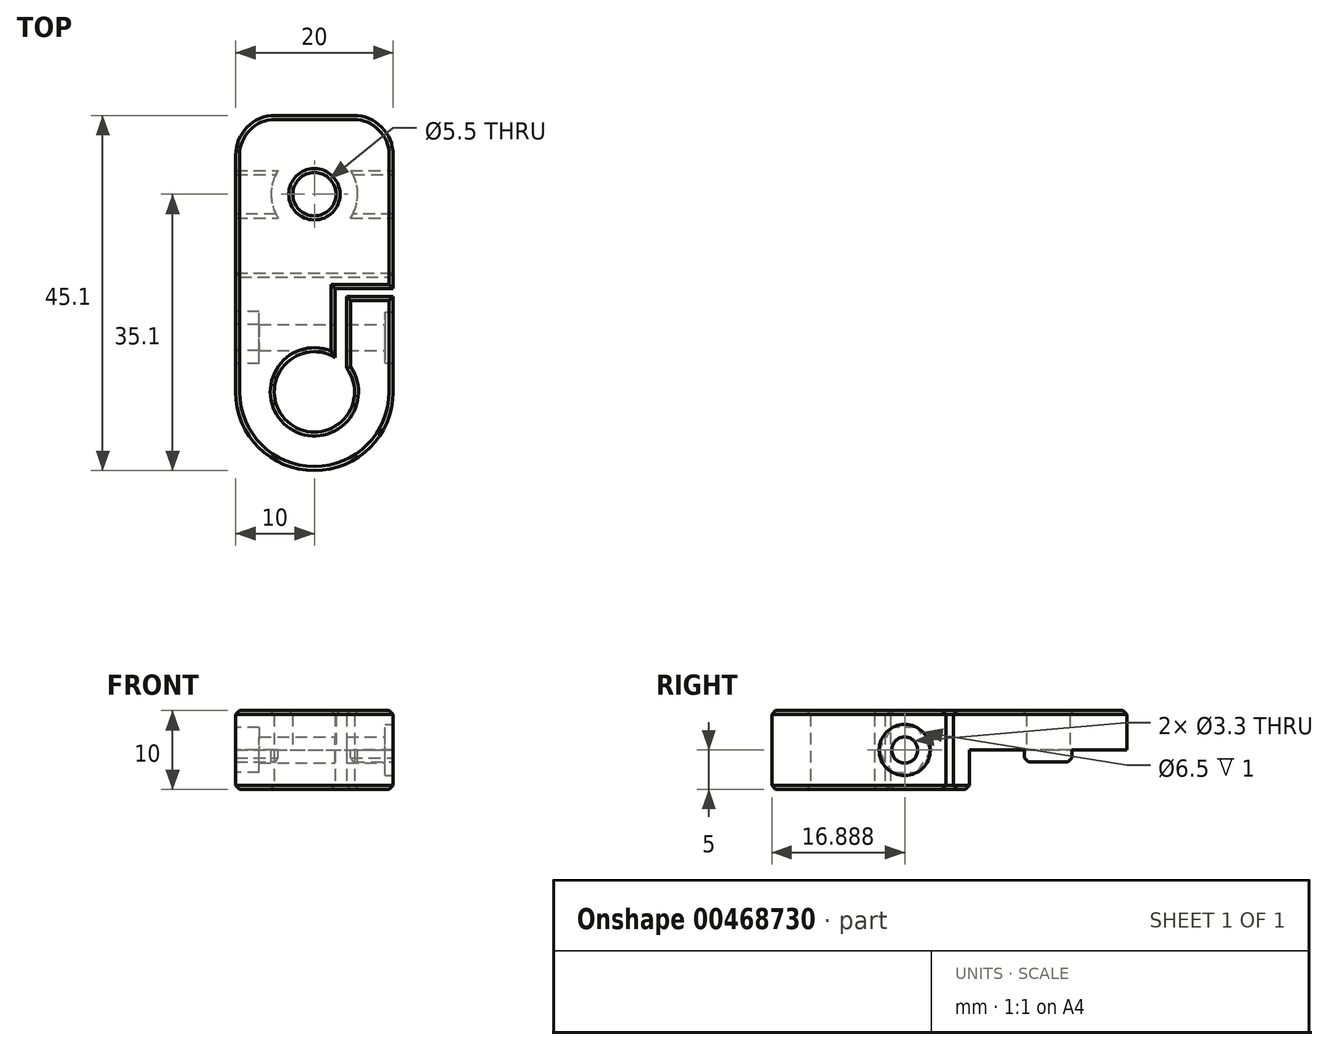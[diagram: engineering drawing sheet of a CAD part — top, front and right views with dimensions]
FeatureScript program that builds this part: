
annotation { "Feature Type Name" : "Feature", "Feature Type Description" : "" }
export const myFeature = defineFeature(function(context is Context, id is Id, definition is map)
    precondition{}
    {
        {
            var Q0;
            Q0=qCreatedBy(makeId("Top.planeOp"),FACE);
            var sketch = newSketch(context, id + "F0", { "sketchPlane" : qUnion([Q0])});
            skLineSegment(sketch, "E0.bottom", {"start": v(-50, 0) * mm, "end": v(50, 0) * mm, "construction": true});
            skLineSegment(sketch, "E0.top", {"start": v(-50, -20) * mm, "end": v(50, -20) * mm, "construction": true});
            skLineSegment(sketch, "E0.left", {"start": v(-50, 0) * mm, "end": v(-50, -20) * mm, "construction": true});
            skLineSegment(sketch, "E0.right", {"start": v(50, 0) * mm, "end": v(50, -20) * mm, "construction": true});
            skLineSegment(sketch, "E1.bottom", {"start": v(-10, 0) * mm, "end": v(10, 0) * mm});
            skLineSegment(sketch, "E1.top", {"start": v(0, -45.1) * mm, "end": v(0, -45.1) * mm});
            skLineSegment(sketch, "E1.left", {"start": v(-10, 0) * mm, "end": v(-10, -35.1) * mm});
            skLineSegment(sketch, "E1.right", {"start": v(10, 0) * mm, "end": v(10, -22) * mm});
            skArc(sketch, "E2", {"start": v(2.6, -30.71) * mm, "mid": v(-3.42, -38.89) * mm, "end": v(4.1, -32.07) * mm});
            skLineSegment(sketch, "E3", {"start": v(-10, -45.1) * mm, "end": v(10, -25.1) * mm, "construction": true});
            skPoint(sketch, "E4.visualSharp", {"position": v(-10, -45.1) * mm});
            skArc(sketch, "E4.filletArc", {"start": v(-10, -35.1) * mm, "mid": v(-7.07, -42.17) * mm, "end": v(0, -45.1) * mm});
            skPoint(sketch, "E5.visualSharp", {"position": v(10, -45.1) * mm});
            skArc(sketch, "E5.filletArc", {"start": v(0, -45.1) * mm, "mid": v(7.07, -42.17) * mm, "end": v(10, -35.1) * mm});
            skLineSegment(sketch, "E6", {"start": v(-10, -45.1) * mm, "end": v(10, -45.1) * mm, "construction": true});
            skLineSegment(sketch, "E7", {"start": v(4.1, -32.07) * mm, "end": v(4.1, -23) * mm});
            skLineSegment(sketch, "E8", {"start": v(4.1, -23) * mm, "end": v(10, -23) * mm});
            skLineSegment(sketch, "E9", {"start": v(10, -22) * mm, "end": v(2.6, -22) * mm});
            skLineSegment(sketch, "E10", {"start": v(2.6, -22) * mm, "end": v(2.6, -30.71) * mm});
            skLineSegment(sketch, "E11.trimOffspring", {"start": v(10, -23) * mm, "end": v(10, -35.1) * mm});
            skSolve(sketch);
        }
        {
            var Q0;
            Q0=makeQuery(id+"F0.imprint","IMPRINT",FACE,{"disambiguationData":[TD([[makeQuery(id+"F0.imprint","IMPRINT",EDGE,{"derivedFrom":sQuery(id+"F0.wireOp",EDGE,"E1.bottom")}),-1.0]])]});
            extrude(context, id + "F1", {"entities" : qUnion([Q0]), "depth" : 5 * mm});
        }
        {
            var Q0;
            Q0=makeQuery(id+"F1.opExtrude","CAP_FACE",FACE,{"disambiguationData":[OSD([sQuery(id+"F0.wireOp",EDGE,"E1.bottom"),sQuery(id+"F0.wireOp",EDGE,"E1.left"),sQuery(id+"F0.wireOp",EDGE,"E1.right"),sQuery(id+"F0.wireOp",EDGE,"E2"),sQuery(id+"F0.wireOp",EDGE,"E4.filletArc"),sQuery(id+"F0.wireOp",EDGE,"E5.filletArc"),sQuery(id+"F0.wireOp",EDGE,"E7"),sQuery(id+"F0.wireOp",EDGE,"E8"),sQuery(id+"F0.wireOp",EDGE,"E9"),sQuery(id+"F0.wireOp",EDGE,"E10"),sQuery(id+"F0.wireOp",EDGE,"E11.trimOffspring")])],"isStart":true});
            var sketch = newSketch(context, id + "F2", { "sketchPlane" : qUnion([Q0])});
            skLineSegment(sketch, "E12.bottom", {"start": v(-10, 0) * mm, "end": v(10, 0) * mm});
            skLineSegment(sketch, "E12.top", {"start": v(-10, 20) * mm, "end": v(10, 20) * mm});
            skLineSegment(sketch, "E12.left", {"start": v(-10, 0) * mm, "end": v(-10, 20) * mm});
            skLineSegment(sketch, "E12.right", {"start": v(10, 0) * mm, "end": v(10, 20) * mm});
            skSolve(sketch);
        }
        {
            var Q0;
            {var subQ2=sQuery(id+"F2.wireOp",EDGE,"E12.top");Q0=makeQuery(id+"F2.imprint","IMPRINT",FACE,{"disambiguationData":[TD([[makeQuery(id+"F2.imprint","IMPRINT",EDGE,{"derivedFrom":subQ2}),1.0]])]});}
            extrude(context, id + "F3", {"entities" : qUnion([Q0]), "operationType" : NewBodyOperationType.ADD, "depth" : 5 * mm});
        }
        {
            var Q0;
            {var subQ0=sQuery(id+"F0.wireOp",EDGE,"E11.trimOffspring");Q0=makeQuery(id+"F3.boolean.opBoolean","MERGE",FACE,{"derivedFrom":[makeQuery(id+"F1.opExtrude","SWEPT_FACE",FACE,{"disambiguationData":[OSD([subQ0])]}),makeQuery(id+"F3.opExtrude","SWEPT_FACE",FACE,{"disambiguationData":[OSD([subQ0])]})]});}
            var sketch = newSketch(context, id + "F4", { "sketchPlane" : qUnion([Q0])});
            skLineSegment(sketch, "E13", {"start": v(-28.21, 5) * mm, "end": v(-28.21, -5) * mm, "construction": true});
            skPoint(sketch, "E14", {"position": v(-28.21, 0) * mm});
            skSolve(sketch);
        }
        {
            var Q0;
            Q0=sQuery(id+"F4.wireOp",VERTEX,"E14");
            var Q1;
            Q1=makeQuery(id+"F1.opExtrude","SWEPT_BODY",BODY,{"disambiguationData":[OSD([sQuery(id+"F0.wireOp",EDGE,"E1.bottom"),sQuery(id+"F0.wireOp",EDGE,"E1.left"),sQuery(id+"F0.wireOp",EDGE,"E1.right"),sQuery(id+"F0.wireOp",EDGE,"E2"),sQuery(id+"F0.wireOp",EDGE,"E4.filletArc"),sQuery(id+"F0.wireOp",EDGE,"E5.filletArc"),sQuery(id+"F0.wireOp",EDGE,"E7"),sQuery(id+"F0.wireOp",EDGE,"E8"),sQuery(id+"F0.wireOp",EDGE,"E9"),sQuery(id+"F0.wireOp",EDGE,"E10"),sQuery(id+"F0.wireOp",EDGE,"E11.trimOffspring")])]});
            hole(context, id + "F5", {"style" : HoleStyle.C_BORE, "endStyle" : HoleEndStyle.BLIND, "holeDiameter" : 3.3 * mm, "cBoreDiameter" : 6.5 * mm, "cBoreDepth" : 1 * mm, "holeDepth" : (22 + 4) * mm, "isTappedThrough" : true, "tappedDepth" : 15 * mm, "tapClearance" : 0, "locations" : qUnion([Q0]), "scope" : qUnion([Q1])});
        }
        {
            var Q0;
            {var subQ0=sQuery(id+"F0.wireOp",EDGE,"E1.left");Q0=makeQuery(id+"F3.boolean.opBoolean","MERGE",FACE,{"derivedFrom":[makeQuery(id+"F1.opExtrude","SWEPT_FACE",FACE,{"disambiguationData":[OSD([subQ0])]}),makeQuery(id+"F3.opExtrude","SWEPT_FACE",FACE,{"disambiguationData":[OSD([subQ0])]})]});}
            var sketch = newSketch(context, id + "F6", { "sketchPlane" : qUnion([Q0])});
            skCircle(sketch, "E15.cCircle", {"center": v(28.21, 0) * mm, "radius": 2.85 * mm, "construction": true});
            skLineSegment(sketch, "E15.0", {"start": v(26.57, -2.85) * mm, "end": v(24.92, 0) * mm});
            skLineSegment(sketch, "E15.1", {"start": v(24.92, 0) * mm, "end": v(26.57, 2.85) * mm});
            skLineSegment(sketch, "E15.2", {"start": v(26.57, 2.85) * mm, "end": v(29.86, 2.85) * mm});
            skLineSegment(sketch, "E15.3", {"start": v(29.86, 2.85) * mm, "end": v(31.5, 0) * mm});
            skLineSegment(sketch, "E15.4", {"start": v(31.5, 0) * mm, "end": v(29.86, -2.85) * mm});
            skLineSegment(sketch, "E15.5", {"start": v(29.86, -2.85) * mm, "end": v(26.57, -2.85) * mm});
            skPoint(sketch, "E15.0.midPoint", {"position": v(25.74, -1.43) * mm});
            skSolve(sketch);
        }
        {
            var Q0;
            Q0=makeQuery(id+"F6.imprint","IMPRINT",FACE,{"disambiguationData":[TD([[makeQuery(id+"F6.imprint","IMPRINT",EDGE,{"derivedFrom":sQuery(id+"F6.wireOp",EDGE,"E15.0")}),-1.0]])]});
            extrude(context, id + "F7", {"entities" : qUnion([Q0]), "operationType" : NewBodyOperationType.REMOVE, "oppositeDirection" : true, "depth" : 3 * mm});
        }
        {
            var Q0;
            Q0=makeQuery(id+"F1.opExtrude","CAP_FACE",FACE,{"disambiguationData":[OSD([sQuery(id+"F0.wireOp",EDGE,"E1.bottom"),sQuery(id+"F0.wireOp",EDGE,"E1.left"),sQuery(id+"F0.wireOp",EDGE,"E1.right"),sQuery(id+"F0.wireOp",EDGE,"E2"),sQuery(id+"F0.wireOp",EDGE,"E4.filletArc"),sQuery(id+"F0.wireOp",EDGE,"E5.filletArc"),sQuery(id+"F0.wireOp",EDGE,"E7"),sQuery(id+"F0.wireOp",EDGE,"E8"),sQuery(id+"F0.wireOp",EDGE,"E9"),sQuery(id+"F0.wireOp",EDGE,"E10"),sQuery(id+"F0.wireOp",EDGE,"E11.trimOffspring")])],"isStart":true});
            var sketch = newSketch(context, id + "F8", { "sketchPlane" : qUnion([Q0])});
            skLineSegment(sketch, "E16", {"start": v(-10, 10) * mm, "end": v(10, 10) * mm, "construction": true});
            skPoint(sketch, "E17", {"position": v(0, 10) * mm});
            skArc(sketch, "E18", {"start": v(-4.6, 13) * mm, "mid": v(-5.5, 10) * mm, "end": v(-4.6, 7) * mm});
            skLineSegment(sketch, "E19.bottom", {"start": v(-10, 13) * mm, "end": v(-4.6, 13) * mm});
            skLineSegment(sketch, "E19.top", {"start": v(-10, 7) * mm, "end": v(-4.6, 7) * mm});
            skLineSegment(sketch, "E19.left", {"start": v(-10, 13) * mm, "end": v(-10, 7) * mm});
            skLineSegment(sketch, "E19.right", {"start": v(10, 13) * mm, "end": v(10, 7) * mm});
            skLineSegment(sketch, "E20.trimOffspring", {"start": v(4.6, 13) * mm, "end": v(10, 13) * mm});
            skLineSegment(sketch, "E21.trimOffspring", {"start": v(4.6, 7) * mm, "end": v(10, 7) * mm});
            skArc(sketch, "E22.trimOffspring", {"start": v(4.6, 7) * mm, "mid": v(5.5, 10) * mm, "end": v(4.6, 13) * mm});
            skSolve(sketch);
        }
        {
            var Q0;
            Q0=makeQuery(id+"F8.imprint","IMPRINT",FACE,{"disambiguationData":[TD([[makeQuery(id+"F8.imprint","IMPRINT",EDGE,{"derivedFrom":sQuery(id+"F8.wireOp",EDGE,"E18")}),-1.0]])]});
            var Q1;
            Q1=makeQuery(id+"F8.imprint","IMPRINT",FACE,{"disambiguationData":[TD([[makeQuery(id+"F8.imprint","IMPRINT",EDGE,{"derivedFrom":sQuery(id+"F8.wireOp",EDGE,"E19.right")}),1.0]])]});
            extrude(context, id + "F9", {"entities" : qUnion([Q0, Q1]), "operationType" : NewBodyOperationType.ADD, "depth" : 1.5 * mm});
        }
        {
            var Q0;
            Q0=sQuery(id+"F8.wireOp",VERTEX,"E17");
            var Q1;
            Q1=makeQuery(id+"F1.opExtrude","SWEPT_BODY",BODY,{"disambiguationData":[OSD([sQuery(id+"F0.wireOp",EDGE,"E1.bottom"),sQuery(id+"F0.wireOp",EDGE,"E1.left"),sQuery(id+"F0.wireOp",EDGE,"E1.right"),sQuery(id+"F0.wireOp",EDGE,"E2"),sQuery(id+"F0.wireOp",EDGE,"E4.filletArc"),sQuery(id+"F0.wireOp",EDGE,"E5.filletArc"),sQuery(id+"F0.wireOp",EDGE,"E7"),sQuery(id+"F0.wireOp",EDGE,"E8"),sQuery(id+"F0.wireOp",EDGE,"E9"),sQuery(id+"F0.wireOp",EDGE,"E10"),sQuery(id+"F0.wireOp",EDGE,"E11.trimOffspring")])]});
            hole(context, id + "F10", {"style" : HoleStyle.SIMPLE, "endStyle" : HoleEndStyle.BLIND, "standardTappedOrClearance" : lookupTablePath({ "standard" : "ISO", "fit" : "Normal", "size" : "M5", "type" : "Clearance" }), "standardBlindInLast" : lookupTablePath({ "fit" : "Standard", "standard" : "ISO", "size" : "M5", "type" : "Clearance" }), "holeDiameter" : 5.5 * mm, "holeDepth" : (22 + 4) * mm, "isTappedThrough" : true, "tappedDepth" : 15 * mm, "tapClearance" : 0, "locations" : qUnion([Q0]), "scope" : qUnion([Q1])});
        }
        {
            var Q0;
            Q0=makeQuery(id+"F9.opExtrude","CAP_EDGE",EDGE,{"disambiguationData":[OSD([sQuery(id+"F8.wireOp",EDGE,"E19.top")])],"isStart":false});
            var Q1;
            Q1=makeQuery(id+"F9.opExtrude","CAP_EDGE",EDGE,{"disambiguationData":[OSD([sQuery(id+"F8.wireOp",EDGE,"E19.bottom")])],"isStart":false});
            var Q2;
            Q2=makeQuery(id+"F9.opExtrude","CAP_EDGE",EDGE,{"disambiguationData":[OSD([sQuery(id+"F8.wireOp",EDGE,"E20.trimOffspring")])],"isStart":false});
            var Q3;
            Q3=makeQuery(id+"F9.opExtrude","CAP_EDGE",EDGE,{"disambiguationData":[OSD([sQuery(id+"F8.wireOp",EDGE,"E21.trimOffspring")])],"isStart":false});
            chamfer(context, id + "F11", {"entities" : qUnion([Q0, Q1, Q2, Q3]), "width" : .5 * mm, "tangentPropagation" : true});
        }
        {
            var Q0;
            Q0=makeQuery(id+"F3.opExtrude","CAP_FACE",FACE,{"disambiguationData":[OSD([sQuery(id+"F0.wireOp",EDGE,"E1.left"),sQuery(id+"F0.wireOp",EDGE,"E1.right"),sQuery(id+"F0.wireOp",EDGE,"E2"),sQuery(id+"F0.wireOp",EDGE,"E4.filletArc"),sQuery(id+"F0.wireOp",EDGE,"E5.filletArc"),sQuery(id+"F0.wireOp",EDGE,"E7"),sQuery(id+"F0.wireOp",EDGE,"E8"),sQuery(id+"F0.wireOp",EDGE,"E9"),sQuery(id+"F0.wireOp",EDGE,"E10"),sQuery(id+"F0.wireOp",EDGE,"E11.trimOffspring"),sQuery(id+"F2.wireOp",EDGE,"E12.top")])],"isStart":false});
            var sketch = newSketch(context, id + "F12", { "sketchPlane" : qUnion([Q0])});
            skLineSegment(sketch, "E23.bottom", {"start": v(-10, 20) * mm, "end": v(10, 20) * mm});
            skLineSegment(sketch, "E23.top", {"start": v(-10, 22) * mm, "end": v(10, 22) * mm});
            skLineSegment(sketch, "E23.left", {"start": v(-10, 20) * mm, "end": v(-10, 22) * mm});
            skLineSegment(sketch, "E23.right", {"start": v(10, 20) * mm, "end": v(10, 22) * mm});
            skSolve(sketch);
        }
        {
            var Q0;
            Q0=makeQuery(id+"F1.opExtrude","SWEPT_EDGE",EDGE,{"disambiguationData":[OSD([sQuery(id+"F0.wireOp",EDGE,"E1.bottom"),sQuery(id+"F0.wireOp",EDGE,"E1.right")])]});
            var Q1;
            Q1=makeQuery(id+"F1.opExtrude","SWEPT_EDGE",EDGE,{"disambiguationData":[OSD([sQuery(id+"F0.wireOp",EDGE,"E1.bottom"),sQuery(id+"F0.wireOp",EDGE,"E1.left")])]});
            fillet(context, id + "F13", {"entities" : qUnion([Q0, Q1]), "radius" : 5 * mm, "tangentPropagation" : true, "allowEdgeOverflow" : false});
        }
        {
            var Q0;
            Q0=makeQuery(id+"F1.opExtrude","CAP_FACE",FACE,{"disambiguationData":[OSD([sQuery(id+"F0.wireOp",EDGE,"E1.bottom"),sQuery(id+"F0.wireOp",EDGE,"E1.left"),sQuery(id+"F0.wireOp",EDGE,"E1.right"),sQuery(id+"F0.wireOp",EDGE,"E2"),sQuery(id+"F0.wireOp",EDGE,"E4.filletArc"),sQuery(id+"F0.wireOp",EDGE,"E5.filletArc"),sQuery(id+"F0.wireOp",EDGE,"E7"),sQuery(id+"F0.wireOp",EDGE,"E8"),sQuery(id+"F0.wireOp",EDGE,"E9"),sQuery(id+"F0.wireOp",EDGE,"E10"),sQuery(id+"F0.wireOp",EDGE,"E11.trimOffspring")])],"isStart":false});
            var Q1;
            Q1=makeQuery(id+"F3.opExtrude","CAP_FACE",FACE,{"disambiguationData":[OSD([sQuery(id+"F0.wireOp",EDGE,"E1.left"),sQuery(id+"F0.wireOp",EDGE,"E1.right"),sQuery(id+"F0.wireOp",EDGE,"E2"),sQuery(id+"F0.wireOp",EDGE,"E4.filletArc"),sQuery(id+"F0.wireOp",EDGE,"E5.filletArc"),sQuery(id+"F0.wireOp",EDGE,"E7"),sQuery(id+"F0.wireOp",EDGE,"E8"),sQuery(id+"F0.wireOp",EDGE,"E9"),sQuery(id+"F0.wireOp",EDGE,"E10"),sQuery(id+"F0.wireOp",EDGE,"E11.trimOffspring"),sQuery(id+"F2.wireOp",EDGE,"E12.top")])],"isStart":false});
            var Q2;
            Q2=makeQuery(id+"FGhrBE7uwkQdKlX_1.opExtrude","CAP_FACE",FACE,{"disambiguationData":[OSD([sQuery(id+"F0.wireOp",EDGE,"E9"),sQuery(id+"F0.wireOp",EDGE,"E10"),sQuery(id+"F12.wireOp",EDGE,"E23.bottom"),sQuery(id+"F12.wireOp",EDGE,"E23.top"),sQuery(id+"F12.wireOp",EDGE,"E23.left"),sQuery(id+"F12.wireOp",EDGE,"E23.right")])],"isStart":false});
            chamfer(context, id + "F14", {"entities" : qUnion([Q0, Q1, Q2]), "width" : .5 * mm, "tangentPropagation" : true});
        }
    });
